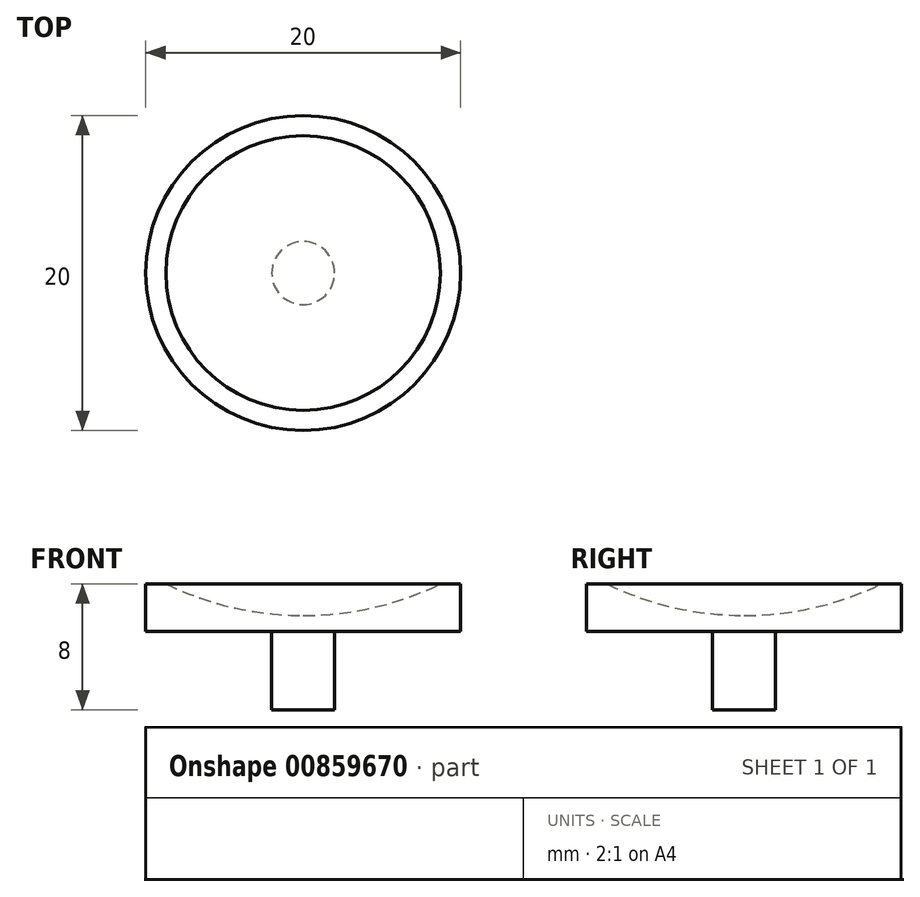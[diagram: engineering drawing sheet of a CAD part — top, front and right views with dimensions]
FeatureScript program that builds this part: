
annotation { "Feature Type Name" : "Feature", "Feature Type Description" : "" }
export const myFeature = defineFeature(function(context is Context, id is Id, definition is map)
    precondition{}
    {
        {
            var Q0;
            Q0=qCreatedBy(makeId("Top.planeOp"),FACE);
            var sketch = newSketch(context, id + "F0", { "sketchPlane" : qUnion([Q0])});
            skCircle(sketch, "E0", {"center": v(0, 0) * mm, "radius": 10 * mm});
            skSolve(sketch);
        }
        {
            var Q0;
            Q0=qSketchRegion(id+"F0",true);
            extrude(context, id + "F1", {"entities" : qUnion([Q0]), "depth" : 3 * mm, "offsetDistance" : 25 * mm});
        }
        {
            var Q0;
            Q0=qCreatedBy(makeId("Front.planeOp"),FACE);
            var sketch = newSketch(context, id + "F2", { "sketchPlane" : qUnion([Q0])});
            skArc(sketch, "E1", {"start": v(0, 41) * mm, "mid": v(-20, 21) * mm, "end": v(0, 1) * mm});
            skLineSegment(sketch, "E2", {"start": v(0, 41) * mm, "end": v(0, 1) * mm});
            skLineSegment(sketch, "E3", {"start": v(0, 68.07) * mm, "end": v(0, -13.2) * mm, "construction": true});
            skSolve(sketch);
        }
        {
            var Q0;
            Q0=qSketchRegion(id+"F2",true);
            var Q1;
            Q1=sQuery(id+"F2.wireOp",EDGE,"E3");
            revolve(context, id + "F3", {"operationType" : NewBodyOperationType.REMOVE, "surfaceOperationType" : NewSurfaceOperationType.NEW, "entities" : qUnion([Q0]), "axis" : qUnion([Q1]), "revolveType" : RevolveType.FULL, "oppositeDirection" : true});
        }
        {
            var Q0;
            Q0=makeQuery(id+"F1.opExtrude","CAP_FACE",FACE,{"disambiguationData":[OSD([sQuery(id+"F0.wireOp",EDGE,"E0")])],"isStart":true});
            var sketch = newSketch(context, id + "F4", { "sketchPlane" : qUnion([Q0])});
            skCircle(sketch, "E4", {"center": v(0, 0) * mm, "radius": 2 * mm});
            skSolve(sketch);
        }
        {
            var Q0;
            Q0=qSketchRegion(id+"F4",true);
            extrude(context, id + "F5", {"entities" : qUnion([Q0]), "operationType" : NewBodyOperationType.ADD, "depth" : 5 * mm, "offsetDistance" : 25 * mm});
        }
    });
